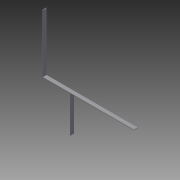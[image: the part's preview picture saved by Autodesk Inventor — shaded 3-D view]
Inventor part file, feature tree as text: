
AUTODESK INVENTOR PART (.ipt)
format: ipt  version: 2013 (Build 170138000, 138)  size: 108,032 bytes
history: native  units: in
note: dims shown in document units (in); Inventor stores cm internally (conversion verified against a paired STEP export)
features: extrude x2, sketch x2
ambient origin geometry x8: Origin, YZ Plane, XZ Plane, XY Plane, X Axis, Y Axis, Z Axis, Center Point
bodies: Solid1 (feature_tree)
feature tree (4):
  extrude  "Extrusion1"  Depth=3.0in
  extrude  "Extrusion2"  Depth=3.0in
  sketch  "Sketch1"  dims[d11=5.0in d12=3.0in]
  sketch  "Sketch2"  dims[d13=2.0in d14=3.0in d15=7.0in d16=0.5in d17=0.125in d18=16.0in d19=25.0in d20=0.125in d21=0.5in d22=0.5in d23=0.125in d24=10.0in d25=4.0in d26=0.0in d27=3.0in d28=0.0in]
